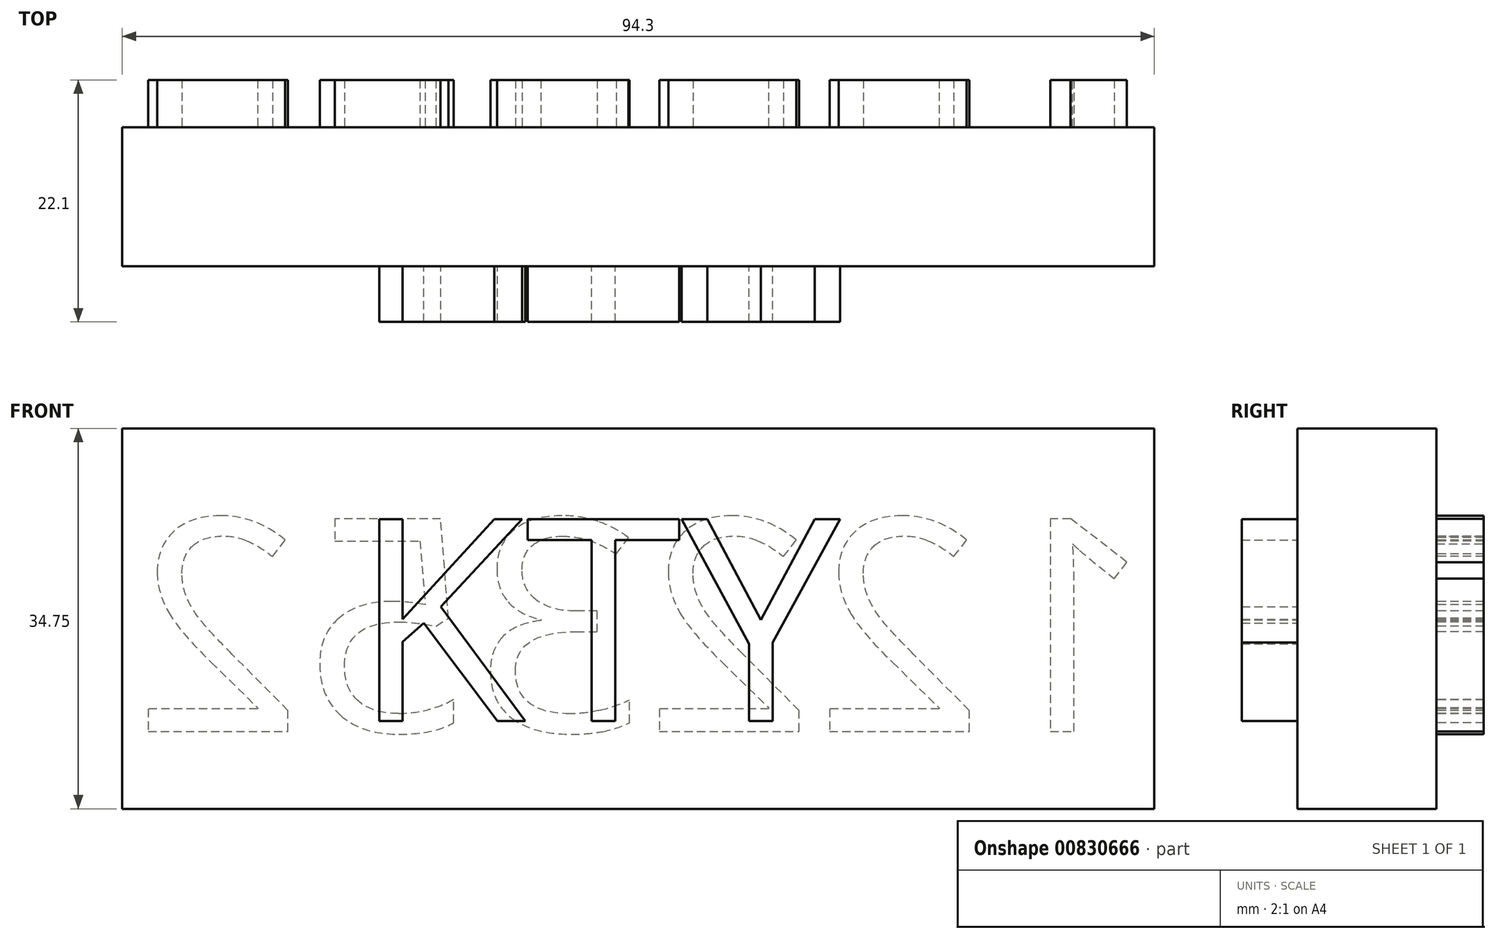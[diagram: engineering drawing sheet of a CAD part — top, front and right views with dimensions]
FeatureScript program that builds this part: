
annotation { "Feature Type Name" : "Feature", "Feature Type Description" : "" }
export const myFeature = defineFeature(function(context is Context, id is Id, definition is map)
    precondition{}
    {
        {
            var Q0;
            Q0=qCreatedBy(makeId("Front.planeOp"),FACE);
            var sketch = newSketch(context, id + "F0", { "sketchPlane" : qUnion([Q0])});
            skLineSegment(sketch, "E0.bottom", {"start": v(0, 0) * mm, "end": v(94.3, 0) * mm});
            skLineSegment(sketch, "E0.top", {"start": v(0, 34.75) * mm, "end": v(94.3, 34.75) * mm});
            skLineSegment(sketch, "E0.left", {"start": v(0, 0) * mm, "end": v(0, 34.75) * mm});
            skLineSegment(sketch, "E0.right", {"start": v(94.3, 0) * mm, "end": v(94.3, 34.75) * mm});
            skSolve(sketch);
        }
        {
            var Q0;
            Q0=makeQuery(id+"F0.imprint","IMPRINT",FACE,{"disambiguationData":[TD([[makeQuery(id+"F0.imprint","IMPRINT",EDGE,{"derivedFrom":sQuery(id+"F0.wireOp",EDGE,"E0.bottom")}),1.0]])]});
            extrude(context, id + "F1", {"entities" : qUnion([Q0]), "depth" : 12.7 * mm, "offsetDistance" : 25.4 * mm});
        }
        {
            var Q0;
            Q0=makeQuery(id+"F1.opExtrude","CAP_FACE",FACE,{"disambiguationData":[OSD([sQuery(id+"F0.wireOp",EDGE,"E0.bottom"),sQuery(id+"F0.wireOp",EDGE,"E0.top"),sQuery(id+"F0.wireOp",EDGE,"E0.left"),sQuery(id+"F0.wireOp",EDGE,"E0.right")])],"isStart":false});
            var sketch = newSketch(context, id + "F2", { "sketchPlane" : qUnion([Q0])});
            skText(sketch, "E1", { "text": "KTY", "fontName": "OpenSans-Regular.ttf"});
            const initialGuessF2  = {"E1": [0.02094, 0.00802, 1, 0, 0.01862]};
            skSetInitialGuess(sketch, initialGuessF2);
            skSolve(sketch);
        }
        {
            var Q0;
            Q0 = qSketchRegion(id + "F2", true);
            extrude(context, id + "F3", {"entities" : qUnion([Q0]), "operationType" : NewBodyOperationType.ADD, "depth" : 5.08 * mm, "offsetDistance" : 25.4 * mm});
        }
        {
            var Q0;
            Q0=makeQuery(id+"F1.opExtrude","CAP_FACE",FACE,{"disambiguationData":[OSD([sQuery(id+"F0.wireOp",EDGE,"E0.bottom"),sQuery(id+"F0.wireOp",EDGE,"E0.top"),sQuery(id+"F0.wireOp",EDGE,"E0.left"),sQuery(id+"F0.wireOp",EDGE,"E0.right")])],"isStart":true});
            var sketch = newSketch(context, id + "F4", { "sketchPlane" : qUnion([Q0])});
            skText(sketch, "E2", { "text": "122352", "fontName": "OpenSans-Regular.ttf"});
            const initialGuessF4  = {"E2": [-0.0943, 0.00708, 1, 0, 0.0196]};
            skSetInitialGuess(sketch, initialGuessF4);
            skSolve(sketch);
        }
        {
            var Q0;
            Q0 = qSketchRegion(id + "F4", true);
            extrude(context, id + "F5", {"entities" : qUnion([Q0]), "operationType" : NewBodyOperationType.ADD, "depth" : 4.32 * mm, "offsetDistance" : 25.4 * mm});
        }
    });
